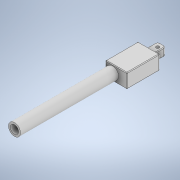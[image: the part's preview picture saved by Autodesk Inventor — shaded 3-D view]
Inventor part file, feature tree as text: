
AUTODESK INVENTOR PART (.ipt)
format: ipt  version: 2021 (Build 250183000, 183)  size: 203,264 bytes
history: native  units: mm
features: sketch x4, extrude x3, fillet x3, hole x1
ambient origin geometry x8: Origin, YZ Plane, XZ Plane, XY Plane, X Axis, Y Axis, Z Axis, Center Point
bodies: Body1 (feature_tree)
feature tree (11):
  extrude  "Extrusion2"  Depth=6.0mm
  extrude  "Extrusion3"  Depth=22.0mm
  extrude  "Extrusion4"  Depth=22.0mm
  fillet  "Fillet1"  Radius=44.0mm
  hole  "Hole1"  [1 undecoded]
  fillet  "Fillet2"  Radius=10.0mm
  fillet  "Fillet3"  Radius=20.0mm
  sketch  "Sketch1"  dims[d0=37.0mm d3=6.0mm]
  sketch  "Sketch3"  dims[d4=300.0mm d5=0.0mm d6=22.0mm]
  sketch  "Sketch5"  dims[d7=22.0mm d8=22.0mm d9=44.0mm]
  sketch  "Sketch6"  dims[d10=100.0mm d11=0.0mm d12=10.0mm d13=10.0mm d14=20.0mm d16=20.0mm d17=40.0mm d18=0.0mm d19=8.0mm d20=15.0mm d21=15.0mm d22=10.0mm d23=6.0mm d24=4.0mm d25=2.0mm d26=90.0deg d27=8.0mm d28=20.594885mm d29=2.0mm d30=2.0mm]
note: 1 required parameter value undecoded (feature->parameter linkage not recoverable at this tier; creation-order binding heuristic only, values carry confidence <= 0.55)
